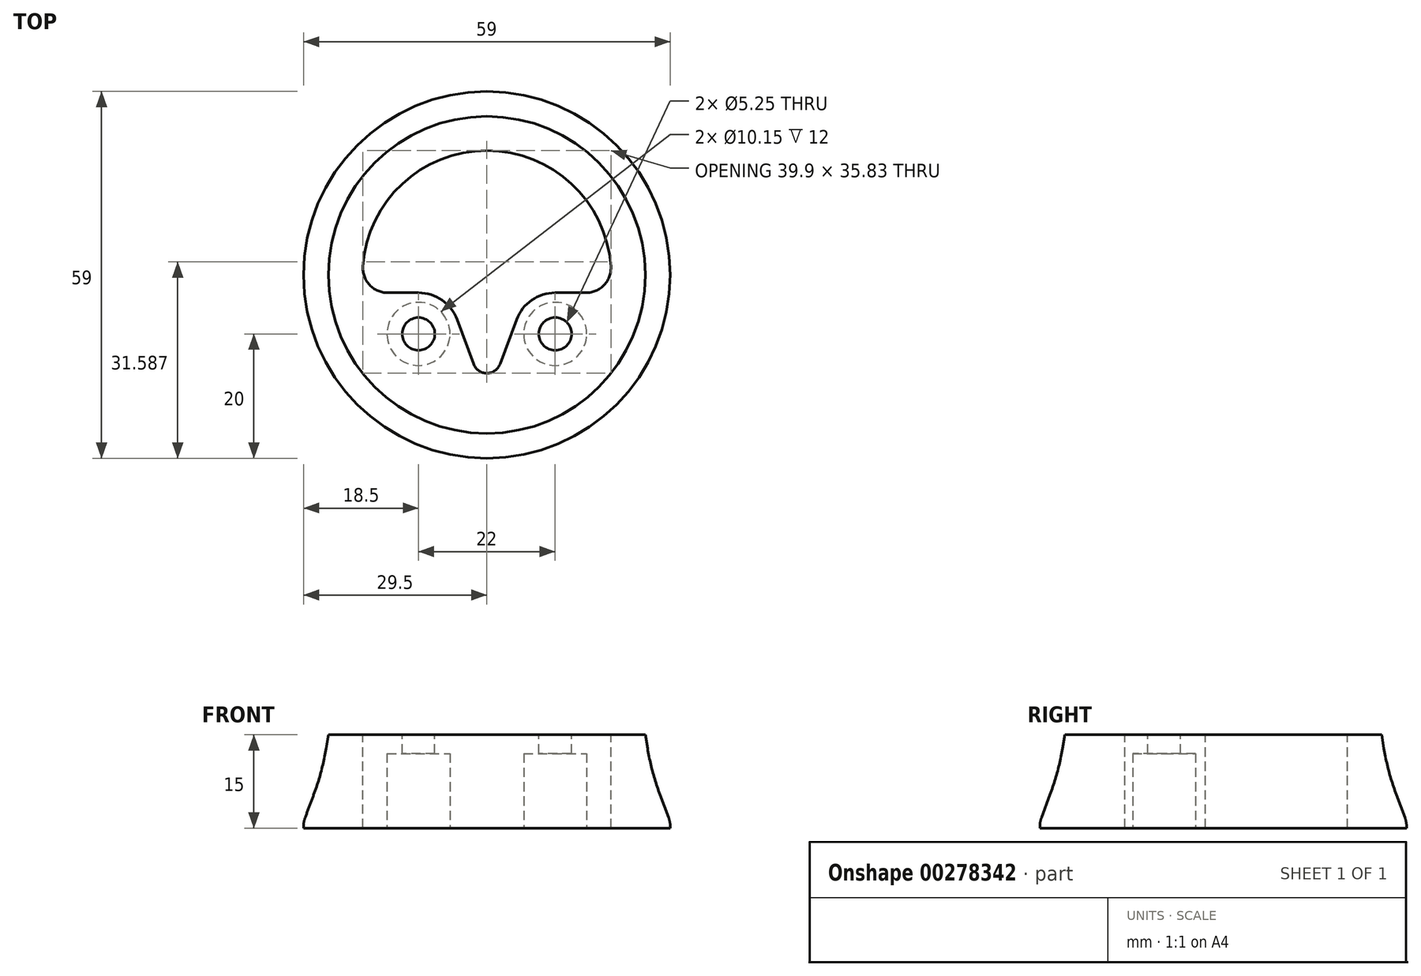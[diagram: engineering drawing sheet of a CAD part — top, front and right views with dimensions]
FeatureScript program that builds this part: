
annotation { "Feature Type Name" : "Feature", "Feature Type Description" : "" }
export const myFeature = defineFeature(function(context is Context, id is Id, definition is map)
    precondition{}
    {
        {
            var Q0;
            Q0=qCreatedBy(makeId("Front.planeOp"),FACE);
            var sketch = newSketch(context, id + "F0", { "sketchPlane" : qUnion([Q0])});
            skLineSegment(sketch, "E0", {"start": v(-29.5, 0) * mm, "end": v(-29.5, 0.27) * mm});
            skLineSegment(sketch, "E1", {"start": v(-29.25, 1.68) * mm, "end": v(-27.86, 5.36) * mm});
            skLineSegment(sketch, "E2", {"start": v(-25.86, 12.83) * mm, "end": v(-25.5, 15) * mm});
            skLineSegment(sketch, "E3", {"start": v(-25.5, 15) * mm, "end": v(0, 15) * mm});
            skLineSegment(sketch, "E4", {"start": v(-29.5, 0) * mm, "end": v(0, 0) * mm});
            skLineSegment(sketch, "E5", {"start": v(0, 0) * mm, "end": v(0, 15) * mm});
            skPoint(sketch, "E6.visualSharp", {"position": v(-26.5, 9) * mm});
            skArc(sketch, "E6.filletArc", {"start": v(-27.86, 5.36) * mm, "mid": v(-26.68, 9.05) * mm, "end": v(-25.86, 12.83) * mm});
            skPoint(sketch, "E7.visualSharp", {"position": v(-29.5, 1) * mm});
            skArc(sketch, "E7.filletArc", {"start": v(-29.25, 1.68) * mm, "mid": v(-29.44, 0.99) * mm, "end": v(-29.5, 0.27) * mm});
            skLineSegment(sketch, "E8", {"start": v(0, 0) * mm, "end": v(0, 42.3) * mm, "construction": true});
            skSolve(sketch);
        }
        {
            var Q0;
            Q0 = qSketchRegion(id + "F0", true);
            var Q1;
            Q1=sQuery(id+"F0.wireOp",EDGE,"E8");
            revolve(context, id + "F1", {"entities" : qUnion([Q0]), "axis" : qUnion([Q1]), "revolveType" : RevolveType.FULL});
        }
        {
            var Q0;
            Q0=makeQuery(id+"F1.opRevolve","SWEPT_FACE",FACE,{"disambiguationData":[OSD([sQuery(id+"F0.wireOp",EDGE,"E3")])]});
            var sketch = newSketch(context, id + "F2", { "sketchPlane" : qUnion([Q0])});
            skArc(sketch, "E9", {"start": v(19.95, 1.4) * mm, "mid": v(0, 20) * mm, "end": v(-19.95, 1.4) * mm});
            skCircle(sketch, "E10", {"center": v(-11, -9.5) * mm, "radius": 2.62 * mm});
            skArc(sketch, "E11", {"start": v(-4.8, -7.18) * mm, "mid": v(-7.22, -4.06) * mm, "end": v(-11, -2.87) * mm});
            skLineSegment(sketch, "E12", {"start": v(-4.8, -7.18) * mm, "end": v(-2.1, -14.36) * mm});
            skLineSegment(sketch, "E13", {"start": v(-11, -2.88) * mm, "end": v(-15.96, -2.88) * mm});
            skPoint(sketch, "E14.visualSharp", {"position": v(-19.8, -2.88) * mm});
            skArc(sketch, "E14.filletArc", {"start": v(-19.95, 1.4) * mm, "mid": v(-18.89, -1.6) * mm, "end": v(-15.96, -2.88) * mm});
            skLineSegment(sketch, "E15", {"start": v(0, 0) * mm, "end": v(0, 20) * mm, "construction": true});
            skArc(sketch, "E16.MirrorCS", {"start": v(19.95, 1.4) * mm, "mid": v(18.89, -1.6) * mm, "end": v(15.96, -2.88) * mm});
            skLineSegment(sketch, "E17.MirrorCS", {"start": v(11, -2.87) * mm, "end": v(15.96, -2.87) * mm});
            skArc(sketch, "E18.MirrorCS", {"start": v(4.8, -7.18) * mm, "mid": v(7.22, -4.06) * mm, "end": v(11, -2.87) * mm});
            skLineSegment(sketch, "E19.MirrorCS", {"start": v(4.8, -7.18) * mm, "end": v(2.1, -14.36) * mm});
            skCircle(sketch, "E20.MirrorC", {"center": v(11, -9.5) * mm, "radius": 2.62 * mm});
            skPoint(sketch, "E21.visualSharp", {"position": v(0, -20) * mm});
            skArc(sketch, "E21.filletArc", {"start": v(-2.1, -14.36) * mm, "mid": v(0, -15.83) * mm, "end": v(2.1, -14.36) * mm});
            skSolve(sketch);
        }
        {
            var Q0;
            Q0 = qSketchRegion(id + "F2", true);
            extrude(context, id + "F3", {"entities" : qUnion([Q0]), "operationType" : NewBodyOperationType.REMOVE, "endBound" : BoundingType.THROUGH_ALL, "oppositeDirection" : true, "depth" : 25 * mm});
        }
        {
            var Q0;
            Q0=makeQuery(id+"F1.opRevolve","SWEPT_FACE",FACE,{"disambiguationData":[OSD([sQuery(id+"F0.wireOp",EDGE,"E4")])]});
            var sketch = newSketch(context, id + "F4", { "sketchPlane" : qUnion([Q0])});
            skCircle(sketch, "E22", {"center": v(-11, 9.5) * mm, "radius": 5.08 * mm});
            skCircle(sketch, "E23", {"center": v(11, 9.5) * mm, "radius": 5.08 * mm});
            skSolve(sketch);
        }
        {
            var Q0;
            Q0=makeQuery(id+"F4.imprint","IMPRINT",FACE,{"disambiguationData":[TD([[makeQuery(id+"F4.imprint","IMPRINT",EDGE,{"derivedFrom":sQuery(id+"F4.wireOp",EDGE,"E23")}),1.0]])]});
            var Q1;
            Q1=makeQuery(id+"F4.imprint","IMPRINT",FACE,{"disambiguationData":[TD([[makeQuery(id+"F4.imprint","IMPRINT",EDGE,{"derivedFrom":sQuery(id+"F4.wireOp",EDGE,"E22")}),1.0]])]});
            extrude(context, id + "F5", {"entities" : qUnion([Q0, Q1]), "operationType" : NewBodyOperationType.REMOVE, "oppositeDirection" : true, "depth" : 12 * mm});
        }
    });
